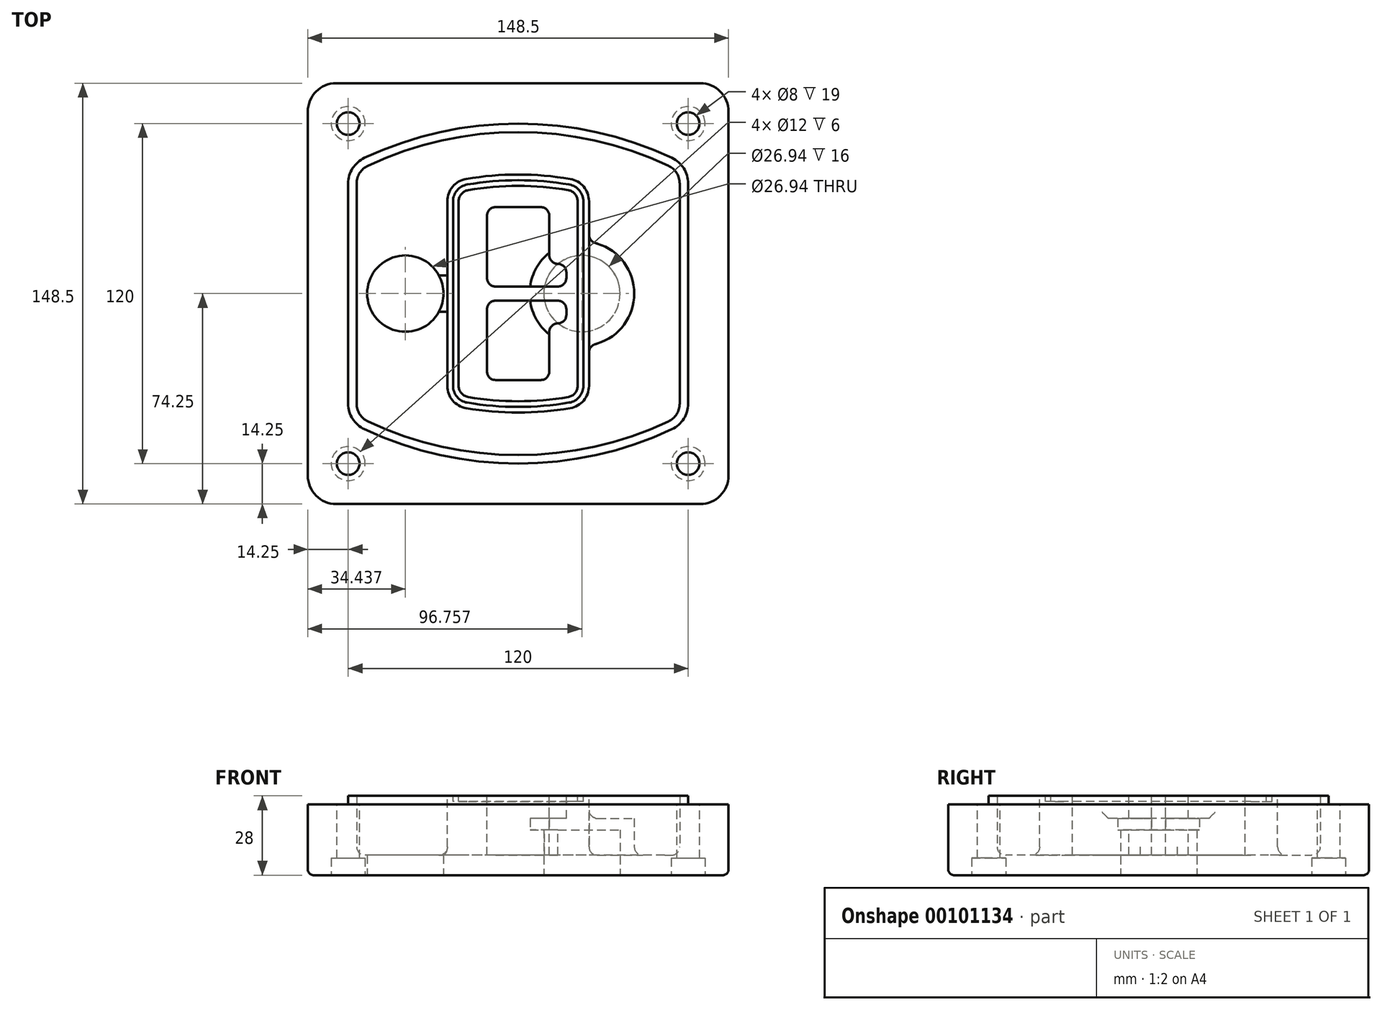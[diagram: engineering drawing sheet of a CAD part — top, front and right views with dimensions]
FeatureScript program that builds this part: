
annotation { "Feature Type Name" : "Feature", "Feature Type Description" : "" }
export const myFeature = defineFeature(function(context is Context, id is Id, definition is map)
    precondition{}
    {
        {
            var Q0;
            Q0=qCreatedBy(makeId("Top.planeOp"),FACE);
            var sketch = newSketch(context, id + "F0", { "sketchPlane" : qUnion([Q0])});
            skPoint(sketch, "E0.rect.middle", {"position": v(0, 0) * mm});
            skLineSegment(sketch, "E1.bottom", {"start": v(-64.25, -74.25) * mm, "end": v(64.25, -74.25) * mm});
            skLineSegment(sketch, "E1.top", {"start": v(-64.25, 74.25) * mm, "end": v(64.25, 74.25) * mm});
            skLineSegment(sketch, "E1.left", {"start": v(-74.25, -64.25) * mm, "end": v(-74.25, 64.25) * mm});
            skLineSegment(sketch, "E1.right", {"start": v(74.25, -64.25) * mm, "end": v(74.25, 64.25) * mm});
            skLineSegment(sketch, "E2", {"start": v(-74.25, 74.25) * mm, "end": v(74.25, -74.25) * mm, "construction": true});
            skLineSegment(sketch, "E3", {"start": v(74.25, 74.25) * mm, "end": v(-74.25, -74.25) * mm, "construction": true});
            skCircle(sketch, "E4", {"center": v(-60, 60) * mm, "radius": 4 * mm});
            skCircle(sketch, "E5", {"center": v(60, 60) * mm, "radius": 4 * mm});
            skCircle(sketch, "E6", {"center": v(60, -60) * mm, "radius": 4 * mm});
            skCircle(sketch, "E7", {"center": v(-60, -60) * mm, "radius": 4 * mm});
            skLineSegment(sketch, "E8", {"start": v(-60, 60) * mm, "end": v(60, 60) * mm, "construction": true});
            skLineSegment(sketch, "E9", {"start": v(60, 60) * mm, "end": v(60, -60) * mm, "construction": true});
            skLineSegment(sketch, "E10", {"start": v(60, -60) * mm, "end": v(-60, -60) * mm, "construction": true});
            skLineSegment(sketch, "E11", {"start": v(-60, -60) * mm, "end": v(-60, 60) * mm, "construction": true});
            skLineSegment(sketch, "E12", {"start": v(-60, 38.83) * mm, "end": v(-60, -38.83) * mm});
            skLineSegment(sketch, "E13", {"start": v(60, 38.83) * mm, "end": v(60, -38.83) * mm});
            skArc(sketch, "E14", {"start": v(54.26, 47.88) * mm, "mid": v(0, 60) * mm, "end": v(-54.26, 47.88) * mm});
            skArc(sketch, "E15", {"start": v(-54.26, -47.88) * mm, "mid": v(0, -60) * mm, "end": v(54.26, -47.88) * mm});
            skLineSegment(sketch, "E16", {"start": v(-60, 0) * mm, "end": v(60, 0) * mm, "construction": true});
            skPoint(sketch, "E17.visualSharp", {"position": v(-60, -45) * mm});
            skArc(sketch, "E17.filletArc", {"start": v(-60, -38.83) * mm, "mid": v(-58.44, -44.2) * mm, "end": v(-54.26, -47.88) * mm});
            skPoint(sketch, "E18.visualSharp", {"position": v(-60, 45) * mm});
            skArc(sketch, "E18.filletArc", {"start": v(-54.26, 47.88) * mm, "mid": v(-58.44, 44.2) * mm, "end": v(-60, 38.83) * mm});
            skPoint(sketch, "E19.visualSharp", {"position": v(60, 45) * mm});
            skArc(sketch, "E19.filletArc", {"start": v(60, 38.83) * mm, "mid": v(58.44, 44.2) * mm, "end": v(54.26, 47.88) * mm});
            skPoint(sketch, "E20.visualSharp", {"position": v(60, -45) * mm});
            skArc(sketch, "E20.filletArc", {"start": v(54.26, -47.88) * mm, "mid": v(58.44, -44.2) * mm, "end": v(60, -38.83) * mm});
            skPoint(sketch, "E21.visualSharp", {"position": v(-74.25, 74.25) * mm});
            skArc(sketch, "E21.filletArc", {"start": v(-64.25, 74.25) * mm, "mid": v(-71.32, 71.32) * mm, "end": v(-74.25, 64.25) * mm});
            skPoint(sketch, "E22.visualSharp", {"position": v(74.25, 74.25) * mm});
            skArc(sketch, "E22.filletArc", {"start": v(74.25, 64.25) * mm, "mid": v(71.32, 71.32) * mm, "end": v(64.25, 74.25) * mm});
            skPoint(sketch, "E23.visualSharp", {"position": v(74.25, -74.25) * mm});
            skArc(sketch, "E23.filletArc", {"start": v(64.25, -74.25) * mm, "mid": v(71.32, -71.32) * mm, "end": v(74.25, -64.25) * mm});
            skPoint(sketch, "E24.visualSharp", {"position": v(-74.25, -74.25) * mm});
            skArc(sketch, "E24.filletArc", {"start": v(-74.25, -64.25) * mm, "mid": v(-71.32, -71.32) * mm, "end": v(-64.25, -74.25) * mm});
            skArc(sketch, "E25.0", {"start": v(57, 38.83) * mm, "mid": v(55.9, 42.58) * mm, "end": v(52.98, 45.17) * mm});
            skLineSegment(sketch, "E25.1", {"start": v(57, 38.83) * mm, "end": v(57, -38.83) * mm});
            skArc(sketch, "E25.2", {"start": v(52.98, -45.17) * mm, "mid": v(55.9, -42.58) * mm, "end": v(57, -38.83) * mm});
            skArc(sketch, "E25.3", {"start": v(-52.98, -45.17) * mm, "mid": v(0, -57) * mm, "end": v(52.98, -45.17) * mm});
            skArc(sketch, "E25.4", {"start": v(-57, -38.83) * mm, "mid": v(-55.9, -42.58) * mm, "end": v(-52.98, -45.17) * mm});
            skArc(sketch, "E25.5", {"start": v(52.98, 45.17) * mm, "mid": v(0, 57) * mm, "end": v(-52.98, 45.17) * mm});
            skLineSegment(sketch, "E25.6", {"start": v(-57, 38.83) * mm, "end": v(-57, -38.83) * mm});
            skArc(sketch, "E25.7", {"start": v(-52.98, 45.17) * mm, "mid": v(-55.9, 42.58) * mm, "end": v(-57, 38.83) * mm});
            skArc(sketch, "E26.0", {"start": v(-55.96, 51.5) * mm, "mid": v(-61.82, 46.33) * mm, "end": v(-64, 38.83) * mm});
            skArc(sketch, "E26.1", {"start": v(55.96, 51.5) * mm, "mid": v(0, 64) * mm, "end": v(-55.96, 51.5) * mm});
            skArc(sketch, "E26.2", {"start": v(64, 38.83) * mm, "mid": v(61.82, 46.33) * mm, "end": v(55.96, 51.5) * mm});
            skLineSegment(sketch, "E26.3", {"start": v(64, 38.83) * mm, "end": v(64, -38.83) * mm});
            skArc(sketch, "E26.4", {"start": v(55.96, -51.5) * mm, "mid": v(61.82, -46.33) * mm, "end": v(64, -38.83) * mm});
            skLineSegment(sketch, "E26.5", {"start": v(-64, 38.83) * mm, "end": v(-64, -38.83) * mm});
            skArc(sketch, "E26.6", {"start": v(-55.96, -51.5) * mm, "mid": v(0, -64) * mm, "end": v(55.96, -51.5) * mm});
            skArc(sketch, "E26.7", {"start": v(-64, -38.83) * mm, "mid": v(-61.82, -46.33) * mm, "end": v(-55.96, -51.5) * mm});
            skSolve(sketch);
        }
        {
            var Q0;
            Q0=makeQuery(id+"F0.imprint","IMPRINT",FACE,{"disambiguationData":[TD([[makeQuery(id+"F0.imprint","IMPRINT",EDGE,{"derivedFrom":sQuery(id+"F0.wireOp",EDGE,"E1.bottom")}),1.0]])]});
            var Q1;
            Q1=makeQuery(id+"F0.imprint","IMPRINT",FACE,{"disambiguationData":[TD([[makeQuery(id+"F0.imprint","IMPRINT",EDGE,{"derivedFrom":sQuery(id+"F0.wireOp",EDGE,"E12")}),1.0]])]});
            var Q2;
            Q2=makeQuery(id+"F0.imprint","IMPRINT",FACE,{"disambiguationData":[TD([[makeQuery(id+"F0.imprint","IMPRINT",EDGE,{"derivedFrom":sQuery(id+"F0.wireOp",EDGE,"E25.0")}),1.0]])]});
            var Q3;
            Q3=makeQuery(id+"F0.imprint","IMPRINT",FACE,{"disambiguationData":[TD([[makeQuery(id+"F0.imprint","IMPRINT",EDGE,{"derivedFrom":sQuery(id+"F0.wireOp",EDGE,"E12")}),-1.0]])]});
            var Q4;
            Q4 = qSketchRegion(id + "F7", true);
            extrude(context, id + "F1", {"entities" : qUnion([Q0, Q1, Q2, Q3, Q4]), "oppositeDirection" : true, "depth" : 25 * mm});
        }
        {
            var Q0;
            Q0=makeQuery(id+"F0.imprint","IMPRINT",FACE,{"disambiguationData":[TD([[makeQuery(id+"F0.imprint","IMPRINT",EDGE,{"derivedFrom":sQuery(id+"F0.wireOp",EDGE,"E12")}),1.0]])]});
            extrude(context, id + "F2", {"entities" : qUnion([Q0]), "operationType" : NewBodyOperationType.ADD, "depth" : 3 * mm});
        }
        {
            var Q0;
            Q0=makeQuery(id+"F0.imprint","IMPRINT",FACE,{"disambiguationData":[TD([[makeQuery(id+"F0.imprint","IMPRINT",EDGE,{"derivedFrom":sQuery(id+"F0.wireOp",EDGE,"E25.0")}),1.0]])]});
            extrude(context, id + "F3", {"entities" : qUnion([Q0]), "operationType" : NewBodyOperationType.REMOVE, "oppositeDirection" : true, "depth" : 18 * mm});
        }
        {
            var Q0;
            Q0=makeQuery(id+"F2.opExtrude","CAP_FACE",FACE,{"disambiguationData":[OSD([sQuery(id+"F0.wireOp",EDGE,"E12"),sQuery(id+"F0.wireOp",EDGE,"E13"),sQuery(id+"F0.wireOp",EDGE,"E14"),sQuery(id+"F0.wireOp",EDGE,"E15"),sQuery(id+"F0.wireOp",EDGE,"E17.filletArc"),sQuery(id+"F0.wireOp",EDGE,"E18.filletArc"),sQuery(id+"F0.wireOp",EDGE,"E19.filletArc"),sQuery(id+"F0.wireOp",EDGE,"E20.filletArc"),sQuery(id+"F0.wireOp",EDGE,"E25.0"),sQuery(id+"F0.wireOp",EDGE,"E25.1"),sQuery(id+"F0.wireOp",EDGE,"E25.2"),sQuery(id+"F0.wireOp",EDGE,"E25.3"),sQuery(id+"F0.wireOp",EDGE,"E25.4"),sQuery(id+"F0.wireOp",EDGE,"E25.5"),sQuery(id+"F0.wireOp",EDGE,"E25.6"),sQuery(id+"F0.wireOp",EDGE,"E25.7")])],"isStart":false});
            var sketch = newSketch(context, id + "F4", { "sketchPlane" : qUnion([Q0])});
            skArc(sketch, "E27.0", {"start": v(-18.34, -40.45) * mm, "mid": v(0, -42) * mm, "end": v(18.34, -40.45) * mm});
            skArc(sketch, "E28.0", {"start": v(18.34, 40.45) * mm, "mid": v(0, 42) * mm, "end": v(-18.34, 40.45) * mm});
            skLineSegment(sketch, "E29", {"start": v(-25, 32.57) * mm, "end": v(-25, -32.57) * mm});
            skLineSegment(sketch, "E30", {"start": v(25, 32.57) * mm, "end": v(25, -32.57) * mm});
            skLineSegment(sketch, "E31", {"start": v(-25, 39.1) * mm, "end": v(25, 39.1) * mm, "construction": true});
            skLineSegment(sketch, "E32", {"start": v(-25, -39.1) * mm, "end": v(25, -39.1) * mm, "construction": true});
            skPoint(sketch, "E33.visualSharp", {"position": v(-25, 39.1) * mm});
            skArc(sketch, "E33.filletArc", {"start": v(-18.34, 40.45) * mm, "mid": v(-23.11, 37.73) * mm, "end": v(-25, 32.57) * mm});
            skPoint(sketch, "E34.visualSharp", {"position": v(25, 39.1) * mm});
            skArc(sketch, "E34.filletArc", {"start": v(25, 32.57) * mm, "mid": v(23.11, 37.73) * mm, "end": v(18.34, 40.45) * mm});
            skPoint(sketch, "E35.visualSharp", {"position": v(25, -39.1) * mm});
            skArc(sketch, "E35.filletArc", {"start": v(18.34, -40.45) * mm, "mid": v(23.11, -37.73) * mm, "end": v(25, -32.57) * mm});
            skPoint(sketch, "E36.visualSharp", {"position": v(-25, -39.1) * mm});
            skArc(sketch, "E36.filletArc", {"start": v(-25, -32.57) * mm, "mid": v(-23.11, -37.73) * mm, "end": v(-18.34, -40.45) * mm});
            skArc(sketch, "E37.0", {"start": v(52.98, 45.17) * mm, "mid": v(0, 57) * mm, "end": v(-52.98, 45.17) * mm});
            skArc(sketch, "E37.1", {"start": v(-52.98, 45.17) * mm, "mid": v(-55.9, 42.58) * mm, "end": v(-57, 38.83) * mm});
            skLineSegment(sketch, "E37.2", {"start": v(-57, 38.83) * mm, "end": v(-57, -38.83) * mm});
            skArc(sketch, "E37.3", {"start": v(-57, -38.83) * mm, "mid": v(-55.9, -42.58) * mm, "end": v(-52.98, -45.17) * mm});
            skArc(sketch, "E37.4", {"start": v(-52.98, -45.17) * mm, "mid": v(0, -57) * mm, "end": v(52.98, -45.17) * mm});
            skArc(sketch, "E37.5", {"start": v(52.98, -45.17) * mm, "mid": v(55.9, -42.58) * mm, "end": v(57, -38.83) * mm});
            skLineSegment(sketch, "E37.6", {"start": v(57, 38.83) * mm, "end": v(57, -38.83) * mm});
            skArc(sketch, "E37.7", {"start": v(57, 38.83) * mm, "mid": v(55.9, 42.58) * mm, "end": v(52.98, 45.17) * mm});
            skLineSegment(sketch, "E38.0", {"start": v(23, 32.57) * mm, "end": v(23, -32.57) * mm});
            skArc(sketch, "E38.1", {"start": v(18, -38.48) * mm, "mid": v(21.58, -36.44) * mm, "end": v(23, -32.57) * mm});
            skArc(sketch, "E38.2", {"start": v(-18, -38.48) * mm, "mid": v(0, -40) * mm, "end": v(18, -38.48) * mm});
            skArc(sketch, "E38.3", {"start": v(-23, -32.57) * mm, "mid": v(-21.58, -36.44) * mm, "end": v(-18, -38.48) * mm});
            skLineSegment(sketch, "E38.4", {"start": v(-23, 32.57) * mm, "end": v(-23, -32.57) * mm});
            skArc(sketch, "E38.5", {"start": v(23, 32.57) * mm, "mid": v(21.58, 36.44) * mm, "end": v(18, 38.48) * mm});
            skArc(sketch, "E38.6", {"start": v(-18, 38.48) * mm, "mid": v(-21.58, 36.44) * mm, "end": v(-23, 32.57) * mm});
            skArc(sketch, "E38.7", {"start": v(18, 38.48) * mm, "mid": v(0, 40) * mm, "end": v(-18, 38.48) * mm});
            skArc(sketch, "E39.0", {"start": v(21, 32.57) * mm, "mid": v(20.06, 35.15) * mm, "end": v(17.67, 36.5) * mm});
            skLineSegment(sketch, "E39.1", {"start": v(21, 32.57) * mm, "end": v(21, -32.57) * mm});
            skArc(sketch, "E39.2", {"start": v(17.67, -36.5) * mm, "mid": v(20.06, -35.15) * mm, "end": v(21, -32.57) * mm});
            skArc(sketch, "E39.3", {"start": v(-17.67, -36.5) * mm, "mid": v(0, -38) * mm, "end": v(17.67, -36.5) * mm});
            skArc(sketch, "E39.4", {"start": v(-21, -32.57) * mm, "mid": v(-20.06, -35.15) * mm, "end": v(-17.67, -36.5) * mm});
            skArc(sketch, "E39.5", {"start": v(17.67, 36.5) * mm, "mid": v(0, 38) * mm, "end": v(-17.67, 36.5) * mm});
            skLineSegment(sketch, "E39.6", {"start": v(-21, 32.57) * mm, "end": v(-21, -32.57) * mm});
            skArc(sketch, "E39.7", {"start": v(-17.67, 36.5) * mm, "mid": v(-20.06, 35.15) * mm, "end": v(-21, 32.57) * mm});
            skLineSegment(sketch, "E40", {"start": v(-25, 0) * mm, "end": v(25, 0) * mm, "construction": true});
            skLineSegment(sketch, "E41", {"start": v(-11, 5.5) * mm, "end": v(-11, 27.5) * mm});
            skLineSegment(sketch, "E42", {"start": v(-8, 30.5) * mm, "end": v(8, 30.5) * mm});
            skLineSegment(sketch, "E43", {"start": v(11, 27.5) * mm, "end": v(11, 13.5) * mm});
            skLineSegment(sketch, "E44", {"start": v(14, 10.5) * mm, "end": v(14, 10.5) * mm});
            skLineSegment(sketch, "E45", {"start": v(17, 7.5) * mm, "end": v(17, 5.5) * mm});
            skLineSegment(sketch, "E46", {"start": v(14, 2.5) * mm, "end": v(-8, 2.5) * mm});
            skPoint(sketch, "E47.visualSharp", {"position": v(-11, 30.5) * mm});
            skArc(sketch, "E47.filletArc", {"start": v(-8, 30.5) * mm, "mid": v(-10.12, 29.62) * mm, "end": v(-11, 27.5) * mm});
            skPoint(sketch, "E48.visualSharp", {"position": v(11, 30.5) * mm});
            skArc(sketch, "E48.filletArc", {"start": v(11, 27.5) * mm, "mid": v(10.12, 29.62) * mm, "end": v(8, 30.5) * mm});
            skPoint(sketch, "E49.visualSharp", {"position": v(11, 10.5) * mm});
            skArc(sketch, "E49.filletArc", {"start": v(11, 13.5) * mm, "mid": v(11.88, 11.38) * mm, "end": v(14, 10.5) * mm});
            skPoint(sketch, "E50.visualSharp", {"position": v(17, 10.5) * mm});
            skArc(sketch, "E50.filletArc", {"start": v(17, 7.5) * mm, "mid": v(16.12, 9.62) * mm, "end": v(14, 10.5) * mm});
            skPoint(sketch, "E51.visualSharp", {"position": v(17, 2.5) * mm});
            skArc(sketch, "E51.filletArc", {"start": v(14, 2.5) * mm, "mid": v(16.12, 3.38) * mm, "end": v(17, 5.5) * mm});
            skPoint(sketch, "E52.visualSharp", {"position": v(-11, 2.5) * mm});
            skArc(sketch, "E52.filletArc", {"start": v(-11, 5.5) * mm, "mid": v(-10.12, 3.38) * mm, "end": v(-8, 2.5) * mm});
            skLineSegment(sketch, "E53.0.MirrorCS", {"start": v(14, -2.5) * mm, "end": v(-8, -2.5) * mm});
            skArc(sketch, "E54.0.MirrorCS", {"start": v(-11, -5.5) * mm, "mid": v(-10.12, -3.38) * mm, "end": v(-8, -2.5) * mm});
            skLineSegment(sketch, "E55.0.MirrorCS", {"start": v(-11, -5.5) * mm, "end": v(-11, -27.5) * mm});
            skArc(sketch, "E56.0.MirrorCS", {"start": v(-8, -30.5) * mm, "mid": v(-10.12, -29.62) * mm, "end": v(-11, -27.5) * mm});
            skLineSegment(sketch, "E57.0.MirrorCS", {"start": v(-8, -30.5) * mm, "end": v(8, -30.5) * mm});
            skArc(sketch, "E58.0.MirrorCS", {"start": v(11, -27.5) * mm, "mid": v(10.12, -29.62) * mm, "end": v(8, -30.5) * mm});
            skLineSegment(sketch, "E59.0.MirrorCS", {"start": v(11, -27.5) * mm, "end": v(11, -13.5) * mm});
            skArc(sketch, "E60.0.MirrorCS", {"start": v(11, -13.5) * mm, "mid": v(11.88, -11.38) * mm, "end": v(14, -10.5) * mm});
            skArc(sketch, "E61.0.MirrorCS", {"start": v(17, -7.5) * mm, "mid": v(16.12, -9.62) * mm, "end": v(14, -10.5) * mm});
            skLineSegment(sketch, "E62.0.MirrorCS", {"start": v(17, -7.5) * mm, "end": v(17, -5.5) * mm});
            skArc(sketch, "E63.0.MirrorCS", {"start": v(14, -2.5) * mm, "mid": v(16.12, -3.38) * mm, "end": v(17, -5.5) * mm});
            skSolve(sketch);
        }
        {
            var Q0;
            Q0=makeQuery(id+"F4.imprint","IMPRINT",FACE,{"disambiguationData":[TD([[makeQuery(id+"F4.imprint","IMPRINT",EDGE,{"derivedFrom":sQuery(id+"F4.wireOp",EDGE,"E27.0")}),1.0]])]});
            var Q1;
            Q1=makeQuery(id+"F4.imprint","IMPRINT",FACE,{"disambiguationData":[TD([[makeQuery(id+"F4.imprint","IMPRINT",EDGE,{"derivedFrom":sQuery(id+"F4.wireOp",EDGE,"E38.0")}),-1.0]])]});
            var Q2;
            Q2=makeQuery(id+"F4.imprint","IMPRINT",FACE,{"disambiguationData":[TD([[makeQuery(id+"F4.imprint","IMPRINT",EDGE,{"derivedFrom":sQuery(id+"F4.wireOp",EDGE,"E39.0")}),1.0]])]});
            extrude(context, id + "F5", {"entities" : qUnion([Q0, Q1, Q2]), "operationType" : NewBodyOperationType.ADD, "endBound" : BoundingType.UP_TO_NEXT, "oppositeDirection" : true, "depth" : 25 * mm});
        }
        {
            var Q0;
            Q0=makeQuery(id+"F4.imprint","IMPRINT",FACE,{"disambiguationData":[TD([[makeQuery(id+"F4.imprint","IMPRINT",EDGE,{"derivedFrom":sQuery(id+"F4.wireOp",EDGE,"E38.0")}),-1.0]])]});
            extrude(context, id + "F6", {"entities" : qUnion([Q0]), "operationType" : NewBodyOperationType.REMOVE, "oppositeDirection" : true, "depth" : 2 * mm});
        }
        {
            var Q0;
            Q0=makeQuery(id+"F1.opExtrude","CAP_FACE",FACE,{"disambiguationData":[OSD([sQuery(id+"F0.wireOp",EDGE,"E1.bottom"),sQuery(id+"F0.wireOp",EDGE,"E1.top"),sQuery(id+"F0.wireOp",EDGE,"E1.left"),sQuery(id+"F0.wireOp",EDGE,"E1.right"),sQuery(id+"F0.wireOp",EDGE,"E4"),sQuery(id+"F0.wireOp",EDGE,"E5"),sQuery(id+"F0.wireOp",EDGE,"E6"),sQuery(id+"F0.wireOp",EDGE,"E7"),sQuery(id+"F0.wireOp",EDGE,"E21.filletArc"),sQuery(id+"F0.wireOp",EDGE,"E22.filletArc"),sQuery(id+"F0.wireOp",EDGE,"E23.filletArc"),sQuery(id+"F0.wireOp",EDGE,"E24.filletArc")])],"isStart":false});
            var sketch = newSketch(context, id + "F7", { "sketchPlane" : qUnion([Q0])});
            skCircle(sketch, "E64", {"center": v(22.5, 0) * mm, "radius": 13.47 * mm});
            skCircle(sketch, "E65", {"center": v(-39.81, 0) * mm, "radius": 13.47 * mm});
            skLineSegment(sketch, "E66", {"start": v(74.25, 0) * mm, "end": v(-74.25, 0) * mm});
            skCircle(sketch, "E67", {"center": v(22.5, 0) * mm, "radius": 18.47 * mm});
            skCircle(sketch, "E68", {"center": v(60, -60) * mm, "radius": 6 * mm});
            skCircle(sketch, "E69", {"center": v(-60, -60) * mm, "radius": 6 * mm});
            skCircle(sketch, "E70", {"center": v(-60, 60) * mm, "radius": 6 * mm});
            skCircle(sketch, "E71", {"center": v(60, 60) * mm, "radius": 6 * mm});
            skSolve(sketch);
        }
        {
            var Q0;
            {var subQ1=sQuery(id+"F7.wireOp",EDGE,"E66");var subQ4=sQuery(id+"F7.wireOp",EDGE,"E64");var subQ6=makeQuery(id+"F7.imprint","INTERSECT",VERTEX,{"disambiguationData":[OD(0.0)],"derivedFrom":[subQ4,subQ1]});Q0=makeQuery(id+"F7.imprint","IMPRINT",FACE,{"disambiguationData":[TD([[makeQuery(id+"F7.imprint","IMPRINT",EDGE,{"disambiguationData":[TD([[subQ6,-1.0]])],"derivedFrom":subQ4}),-1.0]])]});}
            var Q1;
            {var subQ0=sQuery(id+"F7.wireOp",EDGE,"E66");var subQ1=sQuery(id+"F7.wireOp",EDGE,"E64");var subQ3=makeQuery(id+"F7.imprint","INTERSECT",VERTEX,{"disambiguationData":[OD(0.0)],"derivedFrom":[subQ1,subQ0]});Q1=makeQuery(id+"F7.imprint","IMPRINT",FACE,{"disambiguationData":[TD([[makeQuery(id+"F7.imprint","IMPRINT",EDGE,{"disambiguationData":[TD([[subQ3,-1.0]])],"derivedFrom":subQ1}),1.0]])]});}
            var Q2;
            {var subQ0=sQuery(id+"F7.wireOp",EDGE,"E66");var subQ1=sQuery(id+"F7.wireOp",EDGE,"E64");var subQ3=makeQuery(id+"F7.imprint","INTERSECT",VERTEX,{"disambiguationData":[OD(0.0)],"derivedFrom":[subQ1,subQ0]});Q2=makeQuery(id+"F7.imprint","IMPRINT",FACE,{"disambiguationData":[TD([[makeQuery(id+"F7.imprint","IMPRINT",EDGE,{"disambiguationData":[TD([[subQ3,1.0]])],"derivedFrom":subQ1}),1.0]])]});}
            var Q3;
            {var subQ1=sQuery(id+"F7.wireOp",EDGE,"E66");var subQ4=sQuery(id+"F7.wireOp",EDGE,"E64");var subQ6=makeQuery(id+"F7.imprint","INTERSECT",VERTEX,{"disambiguationData":[OD(0.0)],"derivedFrom":[subQ4,subQ1]});Q3=makeQuery(id+"F7.imprint","IMPRINT",FACE,{"disambiguationData":[TD([[makeQuery(id+"F7.imprint","IMPRINT",EDGE,{"disambiguationData":[TD([[subQ6,1.0]])],"derivedFrom":subQ4}),-1.0]])]});}
            extrude(context, id + "F8", {"entities" : qUnion([Q0, Q1, Q2, Q3]), "operationType" : NewBodyOperationType.ADD, "oppositeDirection" : true, "depth" : 20 * mm});
        }
        {
            var Q0;
            {var subQ0=sQuery(id+"F7.wireOp",EDGE,"E66");var subQ1=sQuery(id+"F7.wireOp",EDGE,"E64");var subQ3=makeQuery(id+"F7.imprint","INTERSECT",VERTEX,{"disambiguationData":[OD(0.0)],"derivedFrom":[subQ1,subQ0]});Q0=makeQuery(id+"F7.imprint","IMPRINT",FACE,{"disambiguationData":[TD([[makeQuery(id+"F7.imprint","IMPRINT",EDGE,{"disambiguationData":[TD([[subQ3,-1.0]])],"derivedFrom":subQ1}),1.0]])]});}
            var Q1;
            {var subQ0=sQuery(id+"F7.wireOp",EDGE,"E66");var subQ1=sQuery(id+"F7.wireOp",EDGE,"E64");var subQ3=makeQuery(id+"F7.imprint","INTERSECT",VERTEX,{"disambiguationData":[OD(0.0)],"derivedFrom":[subQ1,subQ0]});Q1=makeQuery(id+"F7.imprint","IMPRINT",FACE,{"disambiguationData":[TD([[makeQuery(id+"F7.imprint","IMPRINT",EDGE,{"disambiguationData":[TD([[subQ3,1.0]])],"derivedFrom":subQ1}),1.0]])]});}
            extrude(context, id + "F9", {"entities" : qUnion([Q0, Q1]), "operationType" : NewBodyOperationType.REMOVE, "oppositeDirection" : true, "depth" : 16 * mm});
        }
        {
            var Q0;
            {var subQ0=sQuery(id+"F7.wireOp",EDGE,"E66");var subQ1=sQuery(id+"F7.wireOp",EDGE,"E65");var subQ3=makeQuery(id+"F7.imprint","INTERSECT",VERTEX,{"disambiguationData":[OD(0.0)],"derivedFrom":[subQ1,subQ0]});Q0=makeQuery(id+"F7.imprint","IMPRINT",FACE,{"disambiguationData":[TD([[makeQuery(id+"F7.imprint","IMPRINT",EDGE,{"disambiguationData":[TD([[subQ3,-1.0]])],"derivedFrom":subQ1}),1.0]])]});}
            var Q1;
            {var subQ0=sQuery(id+"F7.wireOp",EDGE,"E66");var subQ1=sQuery(id+"F7.wireOp",EDGE,"E65");var subQ3=makeQuery(id+"F7.imprint","INTERSECT",VERTEX,{"disambiguationData":[OD(0.0)],"derivedFrom":[subQ1,subQ0]});Q1=makeQuery(id+"F7.imprint","IMPRINT",FACE,{"disambiguationData":[TD([[makeQuery(id+"F7.imprint","IMPRINT",EDGE,{"disambiguationData":[TD([[subQ3,1.0]])],"derivedFrom":subQ1}),1.0]])]});}
            extrude(context, id + "F10", {"entities" : qUnion([Q0, Q1]), "operationType" : NewBodyOperationType.REMOVE, "oppositeDirection" : true, "depth" : 25 * mm});
        }
        {
            var Q0;
            Q0=makeQuery(id+"F7.imprint","IMPRINT",FACE,{"disambiguationData":[TD([[makeQuery(id+"F7.imprint","IMPRINT",EDGE,{"derivedFrom":sQuery(id+"F7.wireOp",EDGE,"E68")}),1.0]])]});
            var Q1;
            Q1=makeQuery(id+"F7.imprint","IMPRINT",FACE,{"disambiguationData":[TD([[makeQuery(id+"F7.imprint","IMPRINT",EDGE,{"derivedFrom":makeQuery(id+"F1.opExtrude","CAP_EDGE",EDGE,{"disambiguationData":[OSD([sQuery(id+"F0.wireOp",EDGE,"E5")])],"isStart":false})}),-1.0]])]});
            var Q2;
            Q2=makeQuery(id+"F7.imprint","IMPRINT",FACE,{"disambiguationData":[TD([[makeQuery(id+"F7.imprint","IMPRINT",EDGE,{"derivedFrom":sQuery(id+"F7.wireOp",EDGE,"E69")}),1.0]])]});
            var Q3;
            Q3=makeQuery(id+"F7.imprint","IMPRINT",FACE,{"disambiguationData":[TD([[makeQuery(id+"F7.imprint","IMPRINT",EDGE,{"derivedFrom":makeQuery(id+"F1.opExtrude","CAP_EDGE",EDGE,{"disambiguationData":[OSD([sQuery(id+"F0.wireOp",EDGE,"E4")])],"isStart":false})}),-1.0]])]});
            var Q4;
            Q4=makeQuery(id+"F7.imprint","IMPRINT",FACE,{"disambiguationData":[TD([[makeQuery(id+"F7.imprint","IMPRINT",EDGE,{"derivedFrom":sQuery(id+"F7.wireOp",EDGE,"E70")}),1.0]])]});
            var Q5;
            Q5=makeQuery(id+"F7.imprint","IMPRINT",FACE,{"disambiguationData":[TD([[makeQuery(id+"F7.imprint","IMPRINT",EDGE,{"derivedFrom":makeQuery(id+"F1.opExtrude","CAP_EDGE",EDGE,{"disambiguationData":[OSD([sQuery(id+"F0.wireOp",EDGE,"E7")])],"isStart":false})}),-1.0]])]});
            var Q6;
            Q6=makeQuery(id+"F7.imprint","IMPRINT",FACE,{"disambiguationData":[TD([[makeQuery(id+"F7.imprint","IMPRINT",EDGE,{"derivedFrom":sQuery(id+"F7.wireOp",EDGE,"E71")}),1.0]])]});
            var Q7;
            Q7=makeQuery(id+"F7.imprint","IMPRINT",FACE,{"disambiguationData":[TD([[makeQuery(id+"F7.imprint","IMPRINT",EDGE,{"derivedFrom":makeQuery(id+"F1.opExtrude","CAP_EDGE",EDGE,{"disambiguationData":[OSD([sQuery(id+"F0.wireOp",EDGE,"E6")])],"isStart":false})}),-1.0]])]});
            extrude(context, id + "F11", {"entities" : qUnion([Q0, Q1, Q2, Q3, Q4, Q5, Q6, Q7]), "operationType" : NewBodyOperationType.REMOVE, "oppositeDirection" : true, "depth" : 6 * mm});
        }
        {
            var Q0;
            Q0=makeQuery(id+"F9.boolean.opBoolean","COPY",FACE,{"derivedFrom":makeQuery(id+"F9.opExtrude","CAP_FACE",FACE,{"disambiguationData":[OSD([sQuery(id+"F7.wireOp",EDGE,"E64")])],"isStart":false})});
            var sketch = newSketch(context, id + "F12", { "sketchPlane" : qUnion([Q0])});
            skArc(sketch, "E72.0", {"start": v(11, 14.45) * mm, "mid": v(6.45, 9.13) * mm, "end": v(4.2, 2.5) * mm});
            skArc(sketch, "E72.1", {"start": v(4.2, -2.5) * mm, "mid": v(6.45, -9.13) * mm, "end": v(11, -14.45) * mm});
            skLineSegment(sketch, "E73", {"start": v(4.2, -2.5) * mm, "end": v(14, -2.5) * mm});
            skLineSegment(sketch, "E74.0", {"start": v(14, 2.5) * mm, "end": v(4.2, 2.5) * mm});
            skArc(sketch, "E74.1", {"start": v(14, 2.5) * mm, "mid": v(16.12, 3.38) * mm, "end": v(17, 5.5) * mm});
            skLineSegment(sketch, "E74.2", {"start": v(17, 7.5) * mm, "end": v(17, 5.5) * mm});
            skArc(sketch, "E74.3", {"start": v(17, 7.5) * mm, "mid": v(16.12, 9.62) * mm, "end": v(14, 10.5) * mm});
            skArc(sketch, "E74.4", {"start": v(11, 13.5) * mm, "mid": v(11.88, 11.38) * mm, "end": v(14, 10.5) * mm});
            skLineSegment(sketch, "E74.5", {"start": v(11, 14.45) * mm, "end": v(11, 13.5) * mm});
            skLineSegment(sketch, "E74.7", {"start": v(14, -2.5) * mm, "end": v(4.2, -2.5) * mm});
            skArc(sketch, "E74.8", {"start": v(14, -2.5) * mm, "mid": v(16.12, -3.38) * mm, "end": v(17, -5.5) * mm});
            skLineSegment(sketch, "E74.9", {"start": v(17, -7.5) * mm, "end": v(17, -5.5) * mm});
            skArc(sketch, "E74.10", {"start": v(17, -7.5) * mm, "mid": v(16.12, -9.62) * mm, "end": v(14, -10.5) * mm});
            skArc(sketch, "E74.11", {"start": v(11, -13.5) * mm, "mid": v(11.88, -11.38) * mm, "end": v(14, -10.5) * mm});
            skLineSegment(sketch, "E74.12", {"start": v(11, -14.45) * mm, "end": v(11, -13.5) * mm});
            skPoint(sketch, "E75.orphan", {"position": v(11, -27.5) * mm});
            skPoint(sketch, "E76.orphan", {"position": v(-8, -2.5) * mm});
            skPoint(sketch, "E77.orphan", {"position": v(-8, 2.5) * mm});
            skPoint(sketch, "E78.orphan", {"position": v(11, 27.5) * mm});
            skSolve(sketch);
        }
        {
            var Q0;
            {var subQ7=sQuery(id+"F12.wireOp",EDGE,"E72.0");var subQ14=sQuery(id+"F12.wireOp",EDGE,"E72.1");var subQ16=sQuery(id+"F12.wireOp",EDGE,"E74.1");var subQ18=sQuery(id+"F12.wireOp",EDGE,"E74.8");Q0=qUnion([makeQuery(id+"F12.imprint","IMPRINT",FACE,{"disambiguationData":[TD([[makeQuery(id+"F12.imprint","IMPRINT",EDGE,{"derivedFrom":subQ7}),1.0]])]}),makeQuery(id+"F12.imprint","IMPRINT",FACE,{"disambiguationData":[TD([[makeQuery(id+"F12.imprint","IMPRINT",EDGE,{"derivedFrom":subQ14}),1.0]])]}),makeQuery(id+"F12.imprint","IMPRINT",FACE,{"disambiguationData":[TD([[makeQuery(id+"F12.imprint","IMPRINT",EDGE,{"derivedFrom":subQ16}),1.0]])]}),makeQuery(id+"F12.imprint","IMPRINT",FACE,{"disambiguationData":[TD([[makeQuery(id+"F12.imprint","IMPRINT",EDGE,{"derivedFrom":subQ18}),-1.0]])]})]);}
            var Q1;
            Q1=makeQuery(id+"F5.boolean.opBoolean","SPLIT",FACE,{"disambiguationData":[TD([makeQuery(id+"F5.opExtrude","SWEPT_FACE",FACE,{"disambiguationData":[OSD([sQuery(id+"F4.wireOp",EDGE,"E41")])]})])],"derivedFrom":makeQuery(id+"F3.boolean.opBoolean","COPY",FACE,{"derivedFrom":makeQuery(id+"F3.opExtrude","CAP_FACE",FACE,{"disambiguationData":[OSD([sQuery(id+"F0.wireOp",EDGE,"E25.0"),sQuery(id+"F0.wireOp",EDGE,"E25.1"),sQuery(id+"F0.wireOp",EDGE,"E25.2"),sQuery(id+"F0.wireOp",EDGE,"E25.3"),sQuery(id+"F0.wireOp",EDGE,"E25.4"),sQuery(id+"F0.wireOp",EDGE,"E25.5"),sQuery(id+"F0.wireOp",EDGE,"E25.6"),sQuery(id+"F0.wireOp",EDGE,"E25.7")])],"isStart":false})})});
            extrude(context, id + "F13", {"entities" : qUnion([Q0]), "operationType" : NewBodyOperationType.REMOVE, "endBound" : BoundingType.UP_TO_SURFACE, "endBoundEntityFace" : qUnion([Q1]), "depth" : 25 * mm});
        }
        {
            var Q0;
            Q0=makeQuery(id+"F3.boolean.opBoolean","COPY",EDGE,{"derivedFrom":makeQuery(id+"F3.opExtrude","CAP_EDGE",EDGE,{"disambiguationData":[OSD([sQuery(id+"F0.wireOp",EDGE,"E25.6")])],"isStart":false})});
            var Q1;
            Q1=makeQuery(id+"F8.boolean.opBoolean","INTERSECT",EDGE,{"derivedFrom":[makeQuery(id+"F5.opExtrude","SWEPT_FACE",FACE,{"disambiguationData":[OSD([sQuery(id+"F4.wireOp",EDGE,"E30")])]}),makeQuery(id+"F8.opExtrude","CAP_FACE",FACE,{"disambiguationData":[OSD([sQuery(id+"F7.wireOp",EDGE,"E67")])],"isStart":false})]});
            var Q2;
            Q2=makeQuery(id+"F8.boolean.opBoolean","INTERSECT",EDGE,{"disambiguationData":[OD(1.0)],"derivedFrom":[makeQuery(id+"F5.opExtrude","SWEPT_FACE",FACE,{"disambiguationData":[OSD([sQuery(id+"F4.wireOp",EDGE,"E30")])]}),makeQuery(id+"F8.opExtrude","SWEPT_FACE",FACE,{"disambiguationData":[OSD([sQuery(id+"F7.wireOp",EDGE,"E67")])]})]});
            var Q3;
            {var subQ0=sQuery(id+"F4.wireOp",EDGE,"E30");Q3=makeQuery(id+"F8.boolean.opBoolean","SPLIT",EDGE,{"disambiguationData":[TD([makeQuery(id+"F5.opExtrude","SWEPT_FACE",FACE,{"disambiguationData":[OSD([sQuery(id+"F4.wireOp",EDGE,"E35.filletArc")])]})])],"derivedFrom":makeQuery(id+"F5.opExtrude","CAP_EDGE",EDGE,{"disambiguationData":[OSD([subQ0])],"isStart":false})});}
            var Q4;
            {var subQ0=sQuery(id+"F0.wireOp",EDGE,"E25.7");var subQ1=sQuery(id+"F0.wireOp",EDGE,"E25.1");var subQ2=sQuery(id+"F0.wireOp",EDGE,"E25.6");var subQ3=sQuery(id+"F0.wireOp",EDGE,"E25.5");var subQ4=sQuery(id+"F0.wireOp",EDGE,"E25.4");var subQ5=sQuery(id+"F0.wireOp",EDGE,"E25.0");var subQ6=sQuery(id+"F0.wireOp",EDGE,"E25.2");var subQ7=sQuery(id+"F0.wireOp",EDGE,"E25.3");Q4=makeQuery(id+"F8.boolean.opBoolean","INTERSECT",EDGE,{"derivedFrom":[makeQuery(id+"F5.boolean.opBoolean","SPLIT",FACE,{"disambiguationData":[TD([makeQuery(id+"F2.opExtrude","SWEPT_FACE",FACE,{"disambiguationData":[OSD([subQ5])]})])],"derivedFrom":makeQuery(id+"F3.boolean.opBoolean","COPY",FACE,{"derivedFrom":makeQuery(id+"F3.opExtrude","CAP_FACE",FACE,{"disambiguationData":[OSD([subQ5,subQ1,subQ6,subQ7,subQ4,subQ3,subQ2,subQ0])],"isStart":false})})}),makeQuery(id+"F8.opExtrude","SWEPT_FACE",FACE,{"disambiguationData":[OSD([sQuery(id+"F7.wireOp",EDGE,"E67")])]})]});}
            var Q5;
            Q5=makeQuery(id+"F8.boolean.opBoolean","INTERSECT",EDGE,{"disambiguationData":[OD(0.0)],"derivedFrom":[makeQuery(id+"F5.opExtrude","SWEPT_FACE",FACE,{"disambiguationData":[OSD([sQuery(id+"F4.wireOp",EDGE,"E30")])]}),makeQuery(id+"F8.opExtrude","SWEPT_FACE",FACE,{"disambiguationData":[OSD([sQuery(id+"F7.wireOp",EDGE,"E67")])]})]});
            fillet(context, id + "F14", {"entities" : qUnion([Q0, Q1, Q2, Q3, Q4, Q5]), "radius" : 3 * mm, "tangentPropagation" : true, "allowEdgeOverflow" : false});
        }
        {
            var Q0;
            Q0=makeQuery(id+"F1.opExtrude","CAP_EDGE",EDGE,{"disambiguationData":[OSD([sQuery(id+"F0.wireOp",EDGE,"E1.bottom")])],"isStart":false});
            fillet(context, id + "F15", {"entities" : qUnion([Q0]), "radius" : 2 * mm, "tangentPropagation" : true, "allowEdgeOverflow" : false});
        }
    });
